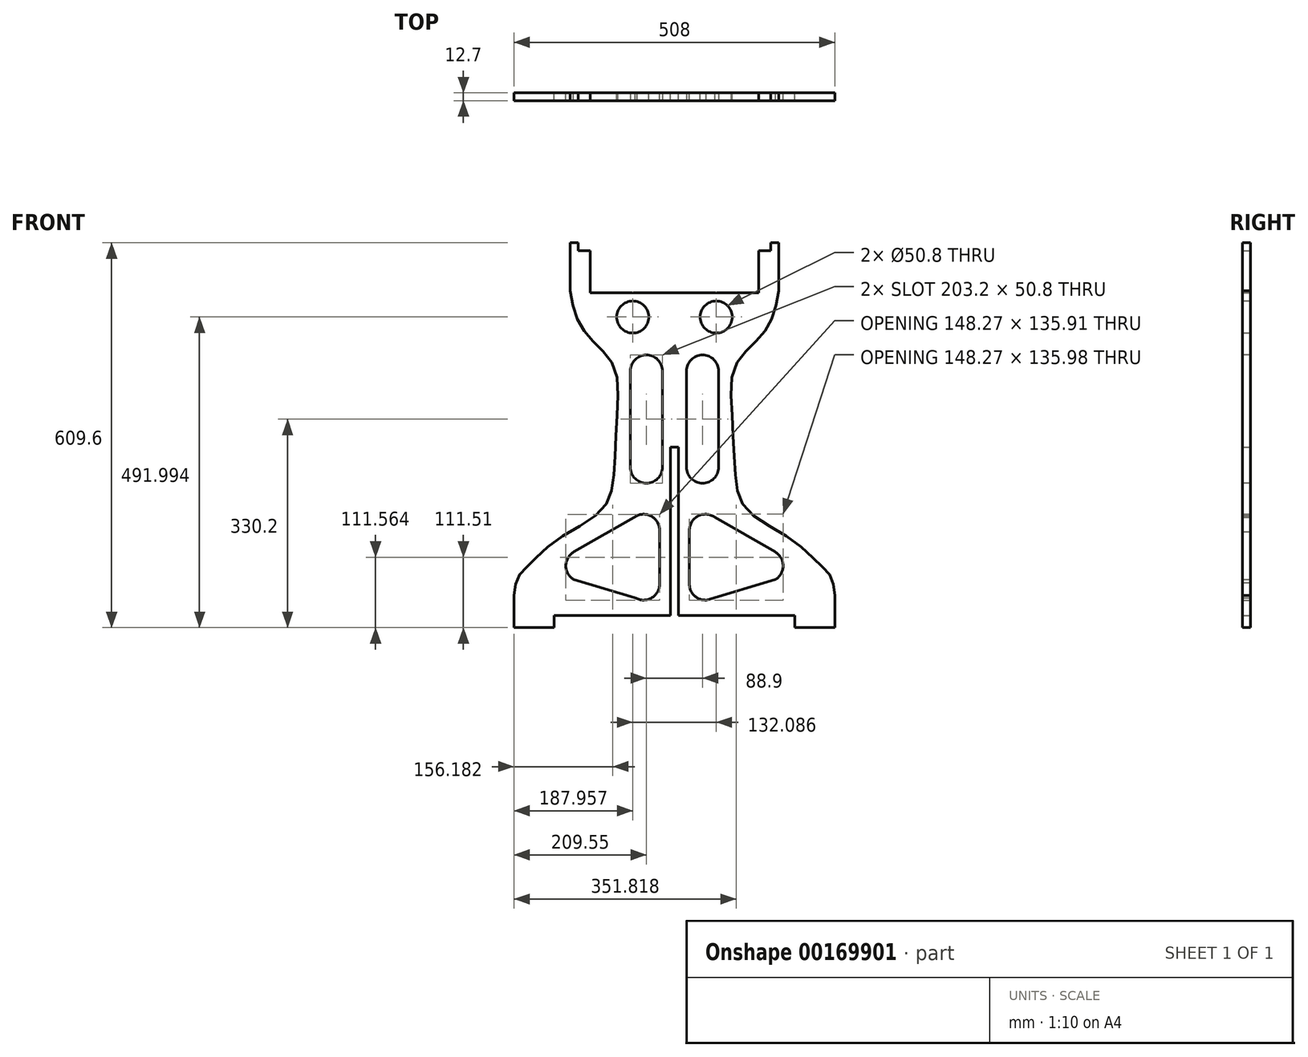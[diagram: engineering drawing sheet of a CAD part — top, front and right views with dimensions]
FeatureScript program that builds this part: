
annotation { "Feature Type Name" : "Feature", "Feature Type Description" : "" }
export const myFeature = defineFeature(function(context is Context, id is Id, definition is map)
    precondition{}
    {
        {
            var Q0;
            Q0=qCreatedBy(makeId("Front.planeOp"),FACE);
            var sketch = newSketch(context, id + "F0", { "sketchPlane" : qUnion([Q0])});
            skLineSegment(sketch, "E0", {"start": v(0, 285.75) * mm, "end": v(0, 530.22) * mm});
            skLineSegment(sketch, "E1", {"start": v(152.4, 609.6) * mm, "end": v(165.1, 609.6) * mm});
            skLineSegment(sketch, "E2", {"start": v(165.1, 609.6) * mm, "end": v(165.1, 533.4) * mm});
            skLineSegment(sketch, "E3", {"start": v(165.1, 609.6) * mm, "end": v(152.4, 609.6) * mm});
            skLineSegment(sketch, "E4", {"start": v(152.4, 609.6) * mm, "end": v(152.4, 596.9) * mm});
            skLineSegment(sketch, "E5", {"start": v(152.4, 596.9) * mm, "end": v(133.35, 596.9) * mm});
            skLineSegment(sketch, "E6", {"start": v(133.35, 596.9) * mm, "end": v(133.35, 530.22) * mm});
            skLineSegment(sketch, "E7", {"start": v(133.35, 530.22) * mm, "end": v(0, 530.22) * mm});
            skLineSegment(sketch, "E8", {"start": v(190.5, 0) * mm, "end": v(254, 0) * mm});
            skLineSegment(sketch, "E9", {"start": v(254, 0) * mm, "end": v(254, 50.8) * mm});
            skLineSegment(sketch, "E10", {"start": v(254, 0) * mm, "end": v(190.5, 0) * mm});
            skLineSegment(sketch, "E11", {"start": v(190.5, 0) * mm, "end": v(190.5, 19.05) * mm});
            skLineSegment(sketch, "E12", {"start": v(190.5, 19.05) * mm, "end": v(6.35, 19.05) * mm});
            skFitSpline(sketch, "E13", {"points": [v(165.1, 533.4) * mm, v(151.94, 484.3) * mm, v(125.02, 449.69) * mm, v(94.25, 409.94) * mm, v(91.68, 327.89) * mm, v(96.81, 235.58) * mm, v(114.76, 186.86) * mm, v(185.28, 139.42) * mm, v(230.15, 99.68) * mm, v(248.1, 79.17) * mm, v(254, 50.8) * mm], "startDerivative": vector(-97.85, -543.75) * mm, "endDerivative": vector(41.55, -423.71) * mm});
            skCircle(sketch, "E14", {"center": v(66.04, 492) * mm, "radius": 25.4 * mm});
            skArc(sketch, "E15", {"start": v(63.82, 174.8) * mm, "mid": v(36.4, 176.26) * mm, "end": v(23.68, 151.93) * mm});
            skArc(sketch, "E16", {"start": v(23.68, 71.21) * mm, "mid": v(30.6, 51.43) * mm, "end": v(50.03, 43.58) * mm});
            skArc(sketch, "E17", {"start": v(160.25, 76.44) * mm, "mid": v(171.96, 98.43) * mm, "end": v(159.24, 119.85) * mm});
            skLineSegment(sketch, "E18", {"start": v(59.37, 177.37) * mm, "end": v(159.24, 119.85) * mm});
            skLineSegment(sketch, "E19", {"start": v(160.25, 76.44) * mm, "end": v(50.03, 43.58) * mm});
            skLineSegment(sketch, "E20", {"start": v(23.68, 156.44) * mm, "end": v(23.68, 66.7) * mm});
            skCircle(sketch, "E21.MirrorC", {"center": v(-66.04, 492) * mm, "radius": 25.4 * mm});
            skLineSegment(sketch, "E22.MirrorCS", {"start": v(-133.35, 530.22) * mm, "end": v(0, 530.22) * mm});
            skLineSegment(sketch, "E23.MirrorCS", {"start": v(-133.35, 596.9) * mm, "end": v(-133.35, 530.22) * mm});
            skLineSegment(sketch, "E24.MirrorCS", {"start": v(-152.4, 596.9) * mm, "end": v(-133.35, 596.9) * mm});
            skLineSegment(sketch, "E25.MirrorCS", {"start": v(-152.4, 609.6) * mm, "end": v(-152.4, 596.9) * mm});
            skLineSegment(sketch, "E26.MirrorCS", {"start": v(-165.1, 609.6) * mm, "end": v(-152.4, 609.6) * mm});
            skLineSegment(sketch, "E27.MirrorCS", {"start": v(-165.1, 609.6) * mm, "end": v(-165.1, 533.4) * mm});
            skFitSpline(sketch, "E28.MirrorCS", {"points": [v(-165.1, 533.4) * mm, v(-151.94, 484.3) * mm, v(-125.02, 449.69) * mm, v(-94.25, 409.94) * mm, v(-91.68, 327.89) * mm, v(-96.81, 235.58) * mm, v(-114.76, 186.86) * mm, v(-185.28, 139.42) * mm, v(-230.15, 99.68) * mm, v(-248.1, 79.17) * mm, v(-254, 50.8) * mm], "startDerivative": vector(97.85, -543.75) * mm, "endDerivative": vector(-41.55, -423.71) * mm});
            skLineSegment(sketch, "E29.MirrorCS", {"start": v(-160.25, 76.44) * mm, "end": v(-62, 47.15) * mm});
            skArc(sketch, "E30.MirrorCS", {"start": v(-160.25, 76.44) * mm, "mid": v(-171.96, 98.43) * mm, "end": v(-159.24, 119.85) * mm});
            skLineSegment(sketch, "E31.MirrorCS", {"start": v(-59.37, 177.37) * mm, "end": v(-159.24, 119.85) * mm});
            skArc(sketch, "E32.MirrorCS", {"start": v(-59.37, 177.37) * mm, "mid": v(-34.24, 174.87) * mm, "end": v(-23.68, 151.93) * mm});
            skLineSegment(sketch, "E33.MirrorCS", {"start": v(-23.68, 151.93) * mm, "end": v(-23.68, 71.21) * mm});
            skArc(sketch, "E34.MirrorCS", {"start": v(-23.68, 71.21) * mm, "mid": v(-35.47, 47.45) * mm, "end": v(-62, 47.15) * mm});
            skLineSegment(sketch, "E35.MirrorCS", {"start": v(-190.5, 19.05) * mm, "end": v(-6.35, 19.05) * mm});
            skLineSegment(sketch, "E36.MirrorCS", {"start": v(-190.5, 0) * mm, "end": v(-190.5, 19.05) * mm});
            skLineSegment(sketch, "E37.MirrorCS", {"start": v(-254, 0) * mm, "end": v(-190.5, 0) * mm});
            skLineSegment(sketch, "E38.MirrorCS", {"start": v(-254, 0) * mm, "end": v(-254, 50.8) * mm});
            skLineSegment(sketch, "E39", {"start": v(6.35, 19.05) * mm, "end": v(6.35, 285.75) * mm});
            skLineSegment(sketch, "E40", {"start": v(6.35, 285.75) * mm, "end": v(-6.35, 285.75) * mm});
            skLineSegment(sketch, "E41", {"start": v(-6.35, 285.75) * mm, "end": v(-6.35, 19.05) * mm});
            skPoint(sketch, "E42.orphan", {"position": v(0, 19.05) * mm});
            skPoint(sketch, "E43.orphan", {"position": v(-50.03, 43.58) * mm});
            skPoint(sketch, "E44.orphan", {"position": v(-23.68, 66.7) * mm});
            skPoint(sketch, "E45.orphan", {"position": v(-63.82, 174.8) * mm});
            skPoint(sketch, "E46.orphan", {"position": v(-23.68, 156.44) * mm});
            skPoint(sketch, "E47.orphan", {"position": v(-146.83, 72.44) * mm});
            skPoint(sketch, "E48.orphan", {"position": v(62, 47.15) * mm});
            skPoint(sketch, "E49.orphan", {"position": v(146.83, 72.44) * mm});
            skSolve(sketch);
        }
        {
            var Q0;
            Q0 = qSketchRegion(id + "F0", true);
            extrude(context, id + "F1", {"entities" : qUnion([Q0]), "depth" : 12.7 * mm});
        }
        {
            var Q0;
            Q0=makeQuery(id+"F1.opExtrude","CAP_FACE",FACE,{"disambiguationData":[OSD([sQuery(id+"F0.wireOp",EDGE,"E2"),sQuery(id+"F0.wireOp",EDGE,"E3"),sQuery(id+"F0.wireOp",EDGE,"E4"),sQuery(id+"F0.wireOp",EDGE,"E5"),sQuery(id+"F0.wireOp",EDGE,"E6"),sQuery(id+"F0.wireOp",EDGE,"E7"),sQuery(id+"F0.wireOp",EDGE,"E9"),sQuery(id+"F0.wireOp",EDGE,"E10"),sQuery(id+"F0.wireOp",EDGE,"E11"),sQuery(id+"F0.wireOp",EDGE,"E12"),sQuery(id+"F0.wireOp",EDGE,"E13"),sQuery(id+"F0.wireOp",EDGE,"E14"),sQuery(id+"F0.wireOp",EDGE,"E15"),sQuery(id+"F0.wireOp",EDGE,"E16"),sQuery(id+"F0.wireOp",EDGE,"E17"),sQuery(id+"F0.wireOp",EDGE,"E18"),sQuery(id+"F0.wireOp",EDGE,"E19"),sQuery(id+"F0.wireOp",EDGE,"E20"),sQuery(id+"F0.wireOp",EDGE,"E21.MirrorC"),sQuery(id+"F0.wireOp",EDGE,"E22.MirrorCS"),sQuery(id+"F0.wireOp",EDGE,"E23.MirrorCS"),sQuery(id+"F0.wireOp",EDGE,"E24.MirrorCS"),sQuery(id+"F0.wireOp",EDGE,"E25.MirrorCS"),sQuery(id+"F0.wireOp",EDGE,"E26.MirrorCS"),sQuery(id+"F0.wireOp",EDGE,"E27.MirrorCS"),sQuery(id+"F0.wireOp",EDGE,"E28.MirrorCS"),sQuery(id+"F0.wireOp",EDGE,"E29.MirrorCS"),sQuery(id+"F0.wireOp",EDGE,"E30.MirrorCS"),sQuery(id+"F0.wireOp",EDGE,"E31.MirrorCS"),sQuery(id+"F0.wireOp",EDGE,"E32.MirrorCS"),sQuery(id+"F0.wireOp",EDGE,"E33.MirrorCS"),sQuery(id+"F0.wireOp",EDGE,"E34.MirrorCS"),sQuery(id+"F0.wireOp",EDGE,"E35.MirrorCS"),sQuery(id+"F0.wireOp",EDGE,"E36.MirrorCS"),sQuery(id+"F0.wireOp",EDGE,"E37.MirrorCS"),sQuery(id+"F0.wireOp",EDGE,"E38.MirrorCS"),sQuery(id+"F0.wireOp",EDGE,"E39"),sQuery(id+"F0.wireOp",EDGE,"E40"),sQuery(id+"F0.wireOp",EDGE,"E41")])],"isStart":false});
            var sketch = newSketch(context, id + "F2", { "sketchPlane" : qUnion([Q0])});
            skLineSegment(sketch, "E50", {"start": v(0, 0) * mm, "end": v(0, 585.35) * mm, "construction": true});
            skArc(sketch, "E51", {"start": v(-19.05, 406.4) * mm, "mid": v(-44.45, 431.8) * mm, "end": v(-69.85, 406.4) * mm});
            skArc(sketch, "E52", {"start": v(-69.85, 254) * mm, "mid": v(-44.45, 228.6) * mm, "end": v(-19.05, 254) * mm});
            skArc(sketch, "E53", {"start": v(69.85, 406.4) * mm, "mid": v(44.45, 431.8) * mm, "end": v(19.05, 406.4) * mm});
            skArc(sketch, "E54", {"start": v(19.05, 254) * mm, "mid": v(44.45, 228.6) * mm, "end": v(69.85, 254) * mm});
            skLineSegment(sketch, "E55", {"start": v(-69.85, 406.4) * mm, "end": v(-69.85, 254) * mm});
            skLineSegment(sketch, "E56", {"start": v(-19.05, 254) * mm, "end": v(-19.05, 406.4) * mm});
            skLineSegment(sketch, "E57", {"start": v(19.05, 406.4) * mm, "end": v(19.05, 254) * mm});
            skLineSegment(sketch, "E58", {"start": v(69.85, 254) * mm, "end": v(69.85, 406.4) * mm});
            skSolve(sketch);
        }
        {
            var Q0;
            Q0 = qSketchRegion(id + "F2", true);
            extrude(context, id + "F3", {"entities" : qUnion([Q0]), "operationType" : NewBodyOperationType.REMOVE, "oppositeDirection" : true, "depth" : 25.4 * mm});
        }
    });
